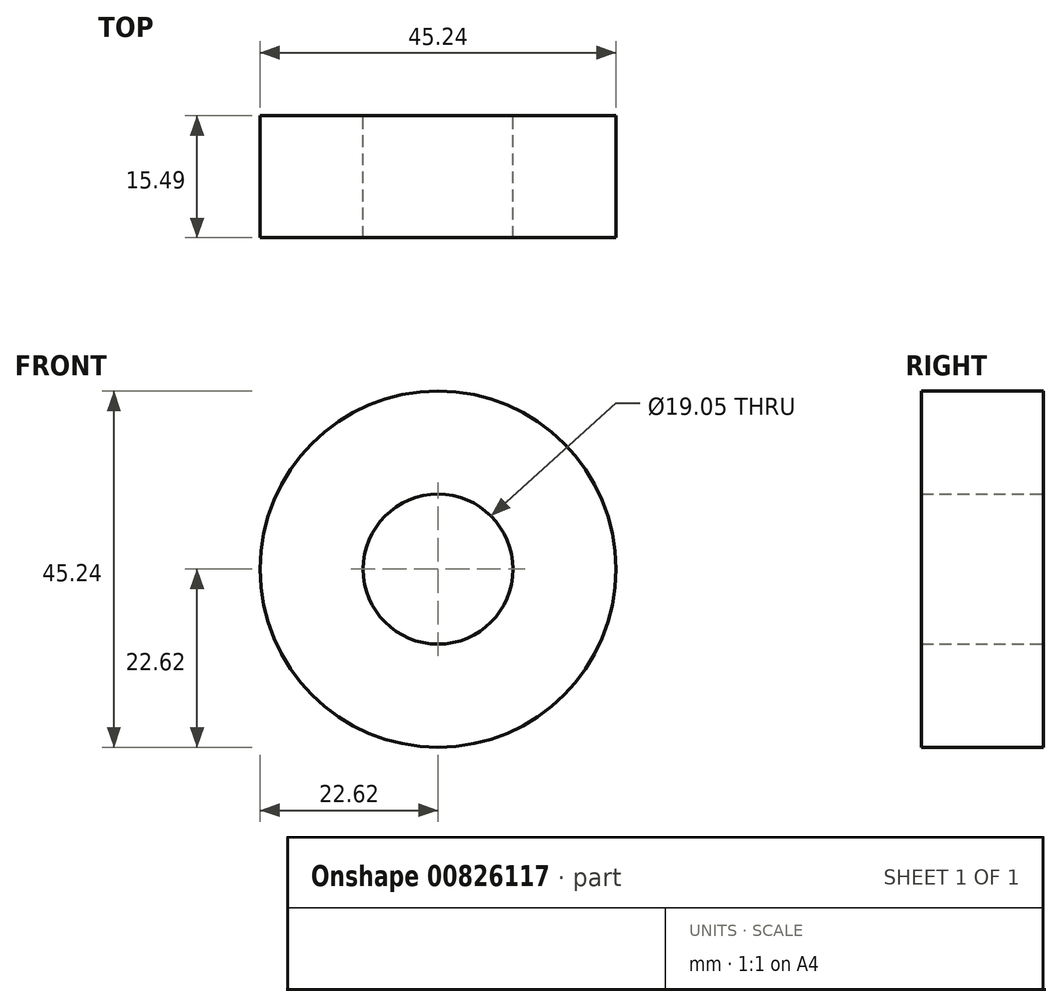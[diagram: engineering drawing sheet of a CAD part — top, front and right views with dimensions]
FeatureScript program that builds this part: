
annotation { "Feature Type Name" : "Feature", "Feature Type Description" : "" }
export const myFeature = defineFeature(function(context is Context, id is Id, definition is map)
    precondition{}
    {
        {
            var Q0;
            Q0=qCreatedBy(makeId("Front.planeOp"),FACE);
            var sketch = newSketch(context, id + "F0", { "sketchPlane" : qUnion([Q0])});
            skCircle(sketch, "E0", {"center": v(0, 0) * mm, "radius": 9.53 * mm});
            skCircle(sketch, "E1", {"center": v(0, 0) * mm, "radius": 22.62 * mm});
            skSolve(sketch);
        }
        {
            var Q0;
            Q0=qSketchRegion(id+"F0",true);
            extrude(context, id + "F1", {"entities" : qUnion([Q0]), "depth" : 15.5 * mm, "offsetDistance" : 25.4 * mm});
        }
    });
